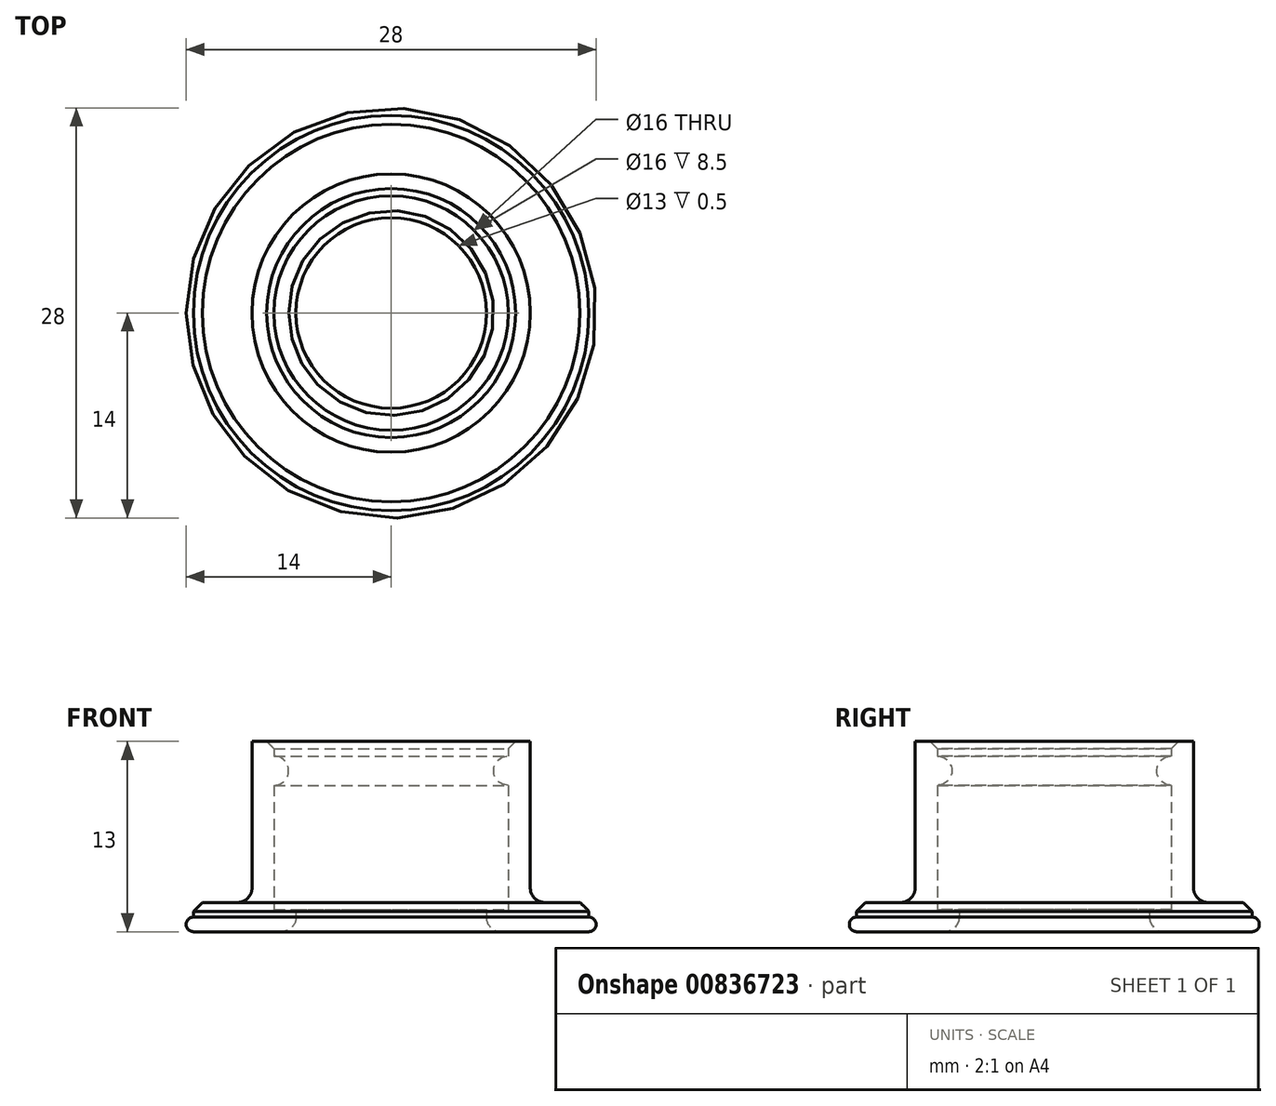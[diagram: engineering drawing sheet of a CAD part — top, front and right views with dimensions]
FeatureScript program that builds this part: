
annotation { "Feature Type Name" : "Feature", "Feature Type Description" : "" }
export const myFeature = defineFeature(function(context is Context, id is Id, definition is map)
    precondition{}
    {
        {
            var Q0;
            Q0=qCreatedBy(makeId("Front.planeOp"),FACE);
            var sketch = newSketch(context, id + "F0", { "sketchPlane" : qUnion([Q0])});
            skLineSegment(sketch, "E0", {"start": v(-13.5, 0) * mm, "end": v(-13.5, 2) * mm});
            skLineSegment(sketch, "E1", {"start": v(-13.5, 0) * mm, "end": v(-8, 0) * mm});
            skLineSegment(sketch, "E2", {"start": v(-8, 0) * mm, "end": v(-8, 10) * mm});
            skLineSegment(sketch, "E3", {"start": v(-8, 12) * mm, "end": v(-8, 12.5) * mm});
            skLineSegment(sketch, "E4", {"start": v(-8, 12.5) * mm, "end": v(-8.5, 13) * mm});
            skLineSegment(sketch, "E5", {"start": v(-9.5, 13) * mm, "end": v(-8.5, 13) * mm});
            skLineSegment(sketch, "E6", {"start": v(-9.5, 13) * mm, "end": v(-9.5, 2) * mm});
            skLineSegment(sketch, "E7", {"start": v(-13.5, 2) * mm, "end": v(-9.5, 2) * mm});
            skArc(sketch, "E8", {"start": v(-8, 10) * mm, "mid": v(-7, 11) * mm, "end": v(-8, 12) * mm});
            skSolve(sketch);
        }
        {
            var Q0;
            Q0=qCreatedBy(makeId("Front.planeOp"),FACE);
            var sketch = newSketch(context, id + "F1", { "sketchPlane" : qUnion([Q0])});
            skLineSegment(sketch, "E9", {"start": v(0, 0) * mm, "end": v(0, 32.34) * mm, "construction": true});
            skSolve(sketch);
        }
        {
            var Q0;
            Q0=makeQuery(id+"F0.imprint","IMPRINT",FACE,{"disambiguationData":[TD([[makeQuery(id+"F0.imprint","IMPRINT",EDGE,{"derivedFrom":sQuery(id+"F0.wireOp",EDGE,"E0")}),-1.0]])]});
            var Q1;
            Q1=sQuery(id+"F1.wireOp",EDGE,"E9");
            revolve(context, id + "F2", {"surfaceOperationType" : NewSurfaceOperationType.NEW, "entities" : qUnion([Q0]), "axis" : qUnion([Q1]), "revolveType" : RevolveType.FULL});
        }
        {
            var Q0;
            Q0=qCreatedBy(makeId("Front.planeOp"),FACE);
            var sketch = newSketch(context, id + "F3", { "sketchPlane" : qUnion([Q0])});
            skLineSegment(sketch, "E10", {"start": v(-13.5, 0) * mm, "end": v(-13.5, 1) * mm});
            skArc(sketch, "E11", {"start": v(-13.5, 1) * mm, "mid": v(-14, 0.5) * mm, "end": v(-13.5, 0) * mm});
            skSolve(sketch);
        }
        {
            var Q0;
            Q0=makeQuery(id+"F3.imprint","IMPRINT",FACE,{"disambiguationData":[TD([[makeQuery(id+"F3.imprint","IMPRINT",EDGE,{"derivedFrom":sQuery(id+"F3.wireOp",EDGE,"E10")}),1.0]])]});
            var Q1;
            Q1=sQuery(id+"F1.wireOp",EDGE,"E9");
            revolve(context, id + "F4", {"operationType" : NewBodyOperationType.ADD, "surfaceOperationType" : NewSurfaceOperationType.NEW, "entities" : qUnion([Q0]), "axis" : qUnion([Q1]), "revolveType" : RevolveType.FULL});
        }
        {
            var Q0;
            Q0=makeQuery(id+"F2.opRevolve","SWEPT_EDGE",EDGE,{"disambiguationData":[OSD([sQuery(id+"F0.wireOp",EDGE,"E0"),sQuery(id+"F0.wireOp",EDGE,"E7")])]});
            chamfer(context, id + "F5", {"entities" : qUnion([Q0]), "width" : 0.6 * mm, "tangentPropagation" : true});
        }
        {
            var Q0;
            Q0=qCreatedBy(makeId("Front.planeOp"),FACE);
            var sketch = newSketch(context, id + "F6", { "sketchPlane" : qUnion([Q0])});
            skLineSegment(sketch, "E12.bottom", {"start": v(-8, 0) * mm, "end": v(-6.5, 0) * mm});
            skLineSegment(sketch, "E12.top", {"start": v(-8, 1.5) * mm, "end": v(-6.5, 1.5) * mm});
            skLineSegment(sketch, "E12.left", {"start": v(-8, 0) * mm, "end": v(-8, 1.5) * mm});
            skLineSegment(sketch, "E12.right", {"start": v(-6.5, 0) * mm, "end": v(-6.5, 1.5) * mm});
            skSolve(sketch);
        }
        {
            var Q0;
            Q0=makeQuery(id+"F6.imprint","IMPRINT",FACE,{"disambiguationData":[TD([[makeQuery(id+"F6.imprint","IMPRINT",EDGE,{"derivedFrom":sQuery(id+"F6.wireOp",EDGE,"E12.bottom")}),1.0]])]});
            var Q1;
            Q1=sQuery(id+"F1.wireOp",EDGE,"E9");
            revolve(context, id + "F7", {"operationType" : NewBodyOperationType.ADD, "surfaceOperationType" : NewSurfaceOperationType.NEW, "entities" : qUnion([Q0]), "axis" : qUnion([Q1]), "revolveType" : RevolveType.FULL});
        }
        {
            var Q0;
            Q0=makeQuery(id+"F2.opRevolve","SWEPT_EDGE",EDGE,{"disambiguationData":[OSD([sQuery(id+"F0.wireOp",EDGE,"E6"),sQuery(id+"F0.wireOp",EDGE,"E7")])]});
            var Q1;
            Q1=makeQuery(id+"F7.opRevolve","SWEPT_EDGE",EDGE,{"disambiguationData":[OSD([sQuery(id+"F6.wireOp",EDGE,"E12.bottom"),sQuery(id+"F6.wireOp",EDGE,"E12.right")])]});
            fillet(context, id + "F8", {"entities" : qUnion([Q0, Q1]), "radius" : 1 * mm, "tangentPropagation" : true, "allowEdgeOverflow" : false});
        }
    });
